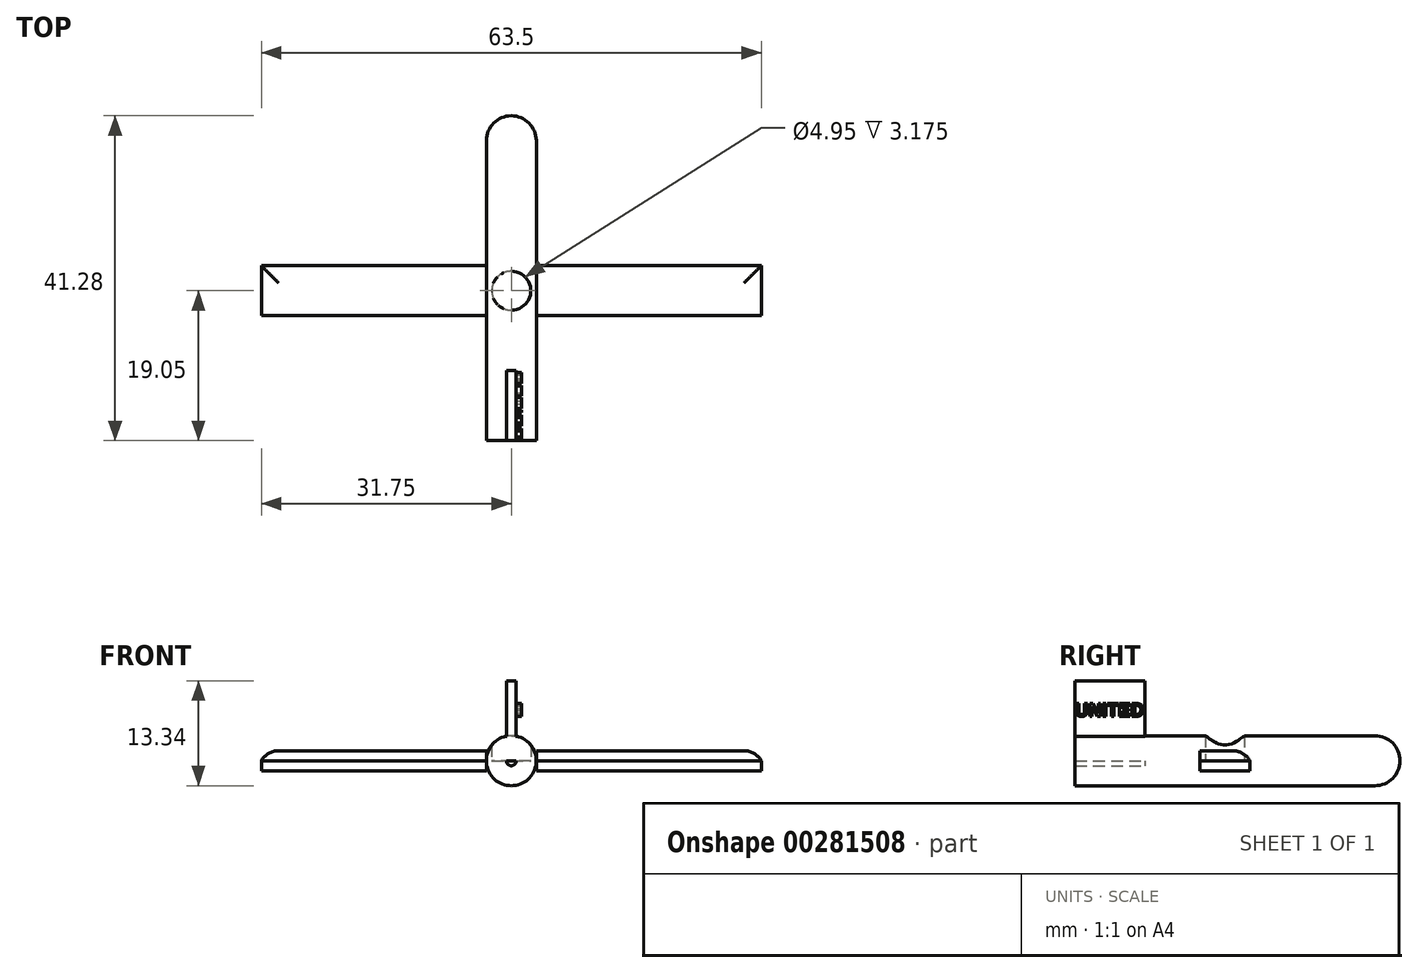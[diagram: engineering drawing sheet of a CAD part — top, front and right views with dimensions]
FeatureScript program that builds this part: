
annotation { "Feature Type Name" : "Feature", "Feature Type Description" : "" }
export const myFeature = defineFeature(function(context is Context, id is Id, definition is map)
    precondition{}
    {
        {
            var Q0;
            Q0=qCreatedBy(makeId("Top.planeOp"),FACE);
            var sketch = newSketch(context, id + "F0", { "sketchPlane" : qUnion([Q0])});
            skLineSegment(sketch, "E0.bottom", {"start": v(3.17, -19.05) * mm, "end": v(-3.18, -19.05) * mm});
            skLineSegment(sketch, "E0.top", {"start": v(3.18, 19.05) * mm, "end": v(-3.17, 19.05) * mm});
            skLineSegment(sketch, "E0.left", {"start": v(3.17, -19.05) * mm, "end": v(3.18, 19.05) * mm});
            skLineSegment(sketch, "E0.right", {"start": v(-3.18, -19.05) * mm, "end": v(-3.17, 19.05) * mm});
            skPoint(sketch, "E0.middle", {"position": v(0, 0) * mm});
            skLineSegment(sketch, "E1.bottom", {"start": v(-31.75, 3.18) * mm, "end": v(31.75, 3.18) * mm});
            skLineSegment(sketch, "E1.top", {"start": v(-31.75, -3.18) * mm, "end": v(31.75, -3.18) * mm});
            skLineSegment(sketch, "E1.left", {"start": v(-31.75, 3.18) * mm, "end": v(-31.75, -3.18) * mm});
            skLineSegment(sketch, "E1.right", {"start": v(31.75, 3.18) * mm, "end": v(31.75, -3.18) * mm});
            skLineSegment(sketch, "E2", {"start": v(0, 19.05) * mm, "end": v(0, -19.05) * mm});
            skLineSegment(sketch, "E3.bottom", {"start": v(-0.63, -19.05) * mm, "end": v(0.64, -19.05) * mm});
            skLineSegment(sketch, "E3.top", {"start": v(-0.64, -10.16) * mm, "end": v(0.63, -10.16) * mm});
            skLineSegment(sketch, "E3.left", {"start": v(-0.63, -19.05) * mm, "end": v(-0.64, -10.16) * mm});
            skLineSegment(sketch, "E3.right", {"start": v(0.64, -19.05) * mm, "end": v(0.63, -10.16) * mm});
            skSolve(sketch);
        }
        {
            var Q0;
            {var subQ0=sQuery(id+"F0.wireOp",EDGE,"E0.right");var subQ1=sQuery(id+"F0.wireOp",EDGE,"E0.top");var subQ2=makeQuery(id+"F0.imprint","INTERSECT",VERTEX,{"derivedFrom":[subQ1,subQ0]});Q0=makeQuery(id+"F0.imprint","IMPRINT",FACE,{"disambiguationData":[TD([[makeQuery(id+"F0.imprint","IMPRINT",EDGE,{"disambiguationData":[TD([[subQ2,1.0]])],"derivedFrom":subQ1}),1.0]])]});}
            var Q1;
            {var subQ0=sQuery(id+"F0.wireOp",EDGE,"E0.right");var subQ1=sQuery(id+"F0.wireOp",EDGE,"E0.bottom");var subQ2=makeQuery(id+"F0.imprint","INTERSECT",VERTEX,{"derivedFrom":[subQ1,subQ0]});Q1=makeQuery(id+"F0.imprint","IMPRINT",FACE,{"disambiguationData":[TD([[makeQuery(id+"F0.imprint","IMPRINT",EDGE,{"disambiguationData":[TD([[subQ2,1.0]])],"derivedFrom":subQ1}),-1.0]])]});}
            var Q2;
            {var subQ0=sQuery(id+"F0.wireOp",EDGE,"E1.top");var subQ1=sQuery(id+"F0.wireOp",EDGE,"E0.right");var subQ2=makeQuery(id+"F0.imprint","INTERSECT",VERTEX,{"derivedFrom":[subQ1,subQ0]});Q2=makeQuery(id+"F0.imprint","IMPRINT",FACE,{"disambiguationData":[TD([[makeQuery(id+"F0.imprint","IMPRINT",EDGE,{"disambiguationData":[TD([[subQ2,-1.0]])],"derivedFrom":subQ1}),-1.0]])]});}
            var Q3;
            Q3=sQuery(id+"F0.wireOp",EDGE,"E2");
            revolve(context, id + "F1", {"entities" : qUnion([Q0, Q1, Q2]), "axis" : qUnion([Q3]), "revolveType" : RevolveType.FULL});
        }
        {
            var Q0;
            {var subQ5=sQuery(id+"F0.wireOp",EDGE,"E1.left");Q0=makeQuery(id+"F0.imprint","IMPRINT",FACE,{"disambiguationData":[TD([[makeQuery(id+"F0.imprint","IMPRINT",EDGE,{"derivedFrom":subQ5}),1.0]])]});}
            var Q1;
            {var subQ5=sQuery(id+"F0.wireOp",EDGE,"E1.right");Q1=makeQuery(id+"F0.imprint","IMPRINT",FACE,{"disambiguationData":[TD([[makeQuery(id+"F0.imprint","IMPRINT",EDGE,{"derivedFrom":subQ5}),-1.0]])]});}
            extrude(context, id + "F2", {"entities" : qUnion([Q0, Q1]), "depth" : 1.27 * mm});
        }
        {
            var Q0;
            {var subQ5=sQuery(id+"F0.wireOp",EDGE,"E3.left");Q0=makeQuery(id+"F0.imprint","IMPRINT",FACE,{"disambiguationData":[TD([[makeQuery(id+"F0.imprint","IMPRINT",EDGE,{"derivedFrom":subQ5}),-1.0]])]});}
            var Q1;
            {var subQ5=sQuery(id+"F0.wireOp",EDGE,"E3.right");Q1=makeQuery(id+"F0.imprint","IMPRINT",FACE,{"disambiguationData":[TD([[makeQuery(id+"F0.imprint","IMPRINT",EDGE,{"derivedFrom":subQ5}),1.0]])]});}
            extrude(context, id + "F3", {"entities" : qUnion([Q0, Q1]), "operationType" : NewBodyOperationType.ADD, "depth" : 10.16 * mm});
        }
        {
            var Q0;
            Q0=qCreatedBy(makeId("Top.planeOp"),FACE);
            var sketch = newSketch(context, id + "F4", { "sketchPlane" : qUnion([Q0])});
            skCircle(sketch, "E4", {"center": v(0, 0) * mm, "radius": 2.48 * mm});
            skSolve(sketch);
        }
        {
            var Q0;
            Q0 = qSketchRegion(id + "F4", true);
            extrude(context, id + "F5", {"entities" : qUnion([Q0]), "operationType" : NewBodyOperationType.REMOVE, "depth" : 6.35 * mm});
        }
        {
            var Q0;
            {var subQ0=sQuery(id+"F0.wireOp",EDGE,"E1.bottom");Q0=makeQuery(id+"F2.opExtrude","CAP_EDGE",EDGE,{"disambiguationData":[OSD([subQ0]),TDD([makeQuery(id+"F0.imprint","IMPRINT",EDGE,{"disambiguationData":[TD([[makeQuery(id+"F0.imprint","INTERSECT",VERTEX,{"derivedFrom":[subQ0,sQuery(id+"F0.wireOp",EDGE,"E1.left")]}),-1.0]])],"derivedFrom":subQ0})])],"isStart":false});}
            var Q1;
            Q1=makeQuery(id+"F2.opExtrude","CAP_EDGE",EDGE,{"disambiguationData":[OSD([sQuery(id+"F0.wireOp",EDGE,"E1.left")])],"isStart":false});
            fillet(context, id + "F6", {"entities" : qUnion([Q0, Q1]), "radius" : 2.54 * mm, "tangentPropagation" : true, "allowEdgeOverflow" : false});
        }
        {
            var Q0;
            Q0=makeQuery(id+"F2.opExtrude","CAP_EDGE",EDGE,{"disambiguationData":[OSD([sQuery(id+"F0.wireOp",EDGE,"E1.right")])],"isStart":false});
            var Q1;
            {var subQ0=sQuery(id+"F0.wireOp",EDGE,"E1.bottom");Q1=makeQuery(id+"F2.opExtrude","CAP_EDGE",EDGE,{"disambiguationData":[OSD([subQ0]),TDD([makeQuery(id+"F0.imprint","IMPRINT",EDGE,{"disambiguationData":[TD([[makeQuery(id+"F0.imprint","INTERSECT",VERTEX,{"derivedFrom":[subQ0,sQuery(id+"F0.wireOp",EDGE,"E1.right")]}),1.0]])],"derivedFrom":subQ0})])],"isStart":false});}
            fillet(context, id + "F7", {"entities" : qUnion([Q0, Q1]), "radius" : 2.54 * mm, "tangentPropagation" : true, "allowEdgeOverflow" : false});
        }
        {
            var Q0;
            Q0=makeQuery(id+"F1.opRevolve","SWEPT_FACE",FACE,{"disambiguationData":[OSD([sQuery(id+"F0.wireOp",EDGE,"E0.top")])]});
            var sketch = newSketch(context, id + "F8", { "sketchPlane" : qUnion([Q0])});
            skCircle(sketch, "E5", {"center": v(0, 0) * mm, "radius": 3.18 * mm});
            skLineSegment(sketch, "E6", {"start": v(-3.18, 0) * mm, "end": v(3.18, 0) * mm});
            skSolve(sketch);
        }
        {
            var Q0;
            {var subQ0=sQuery(id+"F8.wireOp",EDGE,"E6");Q0=makeQuery(id+"F8.imprint","IMPRINT",FACE,{"disambiguationData":[TD([[makeQuery(id+"F8.imprint","IMPRINT",EDGE,{"derivedFrom":subQ0}),1.0]])]});}
            var Q1;
            Q1=sQuery(id+"F8.wireOp",EDGE,"E6");
            revolve(context, id + "F9", {"operationType" : NewBodyOperationType.ADD, "entities" : qUnion([Q0]), "axis" : qUnion([Q1]), "revolveType" : RevolveType.FULL});
        }
        {
            var Q0;
            Q0=makeQuery(id+"F3.opExtrude","SWEPT_FACE",FACE,{"disambiguationData":[OSD([sQuery(id+"F0.wireOp",EDGE,"E3.right")])]});
            var sketch = newSketch(context, id + "F10", { "sketchPlane" : qUnion([Q0])});
            skText(sketch, "E7", { "text": "UNITED", "fontName": "Arimo-Bold.ttf"});
            const initialGuessF10  = {"E7": [-0.01905, 0.00565, 1, 0, 0.0017]};
            skSetInitialGuess(sketch, initialGuessF10);
            skSolve(sketch);
        }
        {
            var Q0;
            Q0 = qSketchRegion(id + "F10", true);
            extrude(context, id + "F11", {"entities" : qUnion([Q0]), "operationType" : NewBodyOperationType.ADD, "depth" : 0.64 * mm});
        }
        {
            var Q0;
            {var subQ5=sQuery(id+"F0.wireOp",EDGE,"E1.right");Q0=makeQuery(id+"F0.imprint","IMPRINT",FACE,{"disambiguationData":[TD([[makeQuery(id+"F0.imprint","IMPRINT",EDGE,{"derivedFrom":subQ5}),-1.0]])]});}
            var Q1;
            {var subQ5=sQuery(id+"F0.wireOp",EDGE,"E1.left");Q1=makeQuery(id+"F0.imprint","IMPRINT",FACE,{"disambiguationData":[TD([[makeQuery(id+"F0.imprint","IMPRINT",EDGE,{"derivedFrom":subQ5}),1.0]])]});}
            extrude(context, id + "F12", {"entities" : qUnion([Q0, Q1]), "oppositeDirection" : true, "depth" : 1.27 * mm});
        }
    });
